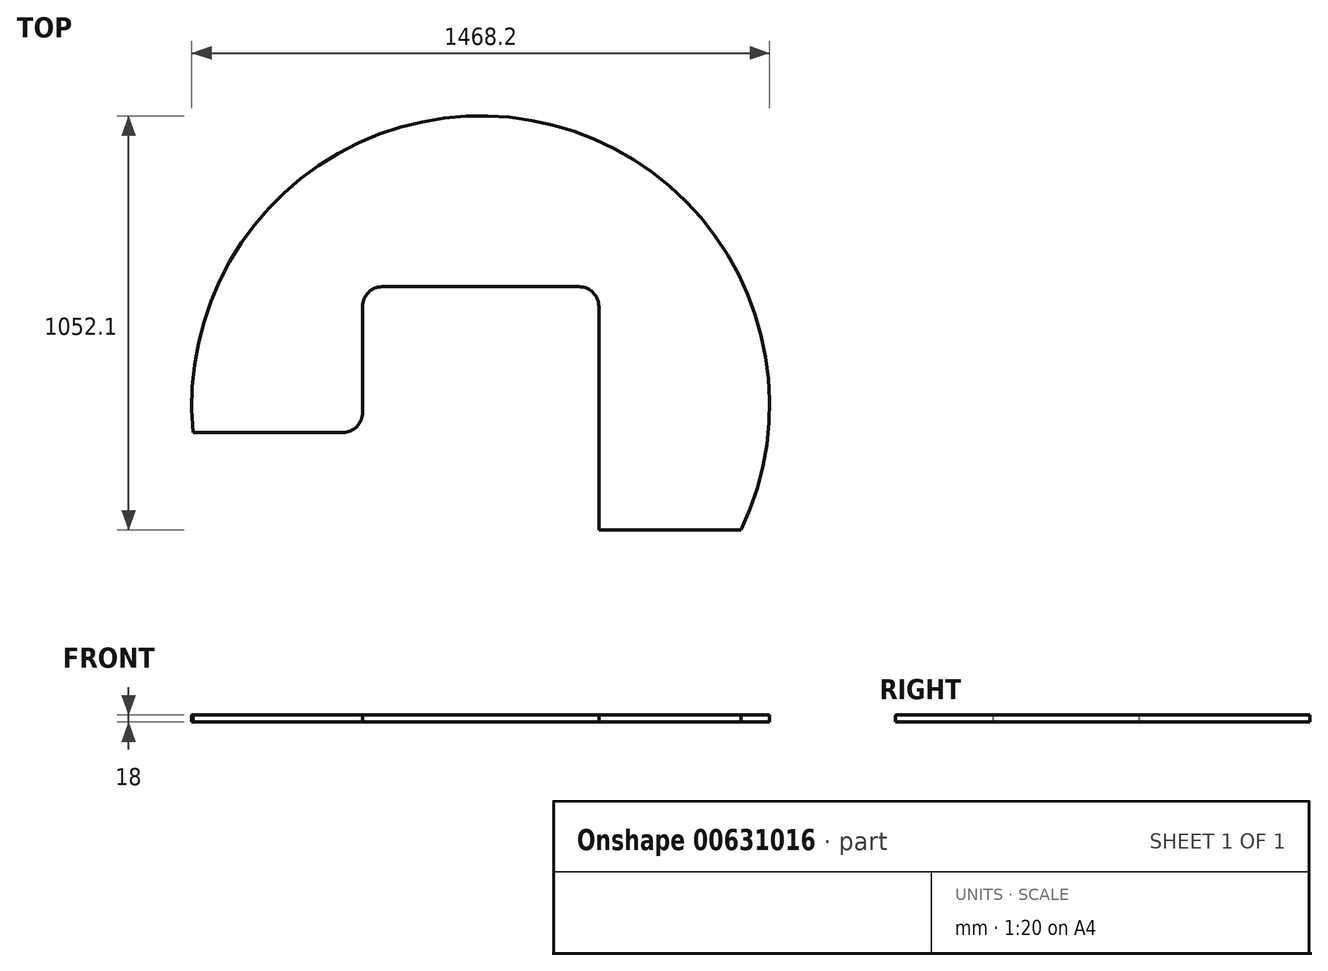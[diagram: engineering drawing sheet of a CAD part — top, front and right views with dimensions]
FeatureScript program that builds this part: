
annotation { "Feature Type Name" : "Feature", "Feature Type Description" : "" }
export const myFeature = defineFeature(function(context is Context, id is Id, definition is map)
    precondition{}
    {
        {
            var Q0;
            Q0=qCreatedBy(makeId("Top.planeOp"),FACE);
            var sketch = newSketch(context, id + "F0", { "sketchPlane" : qUnion([Q0])});
            skLineSegment(sketch, "E0.top", {"start": v(-250, 300) * mm, "end": v(250, 300) * mm});
            skLineSegment(sketch, "E0.left", {"start": v(-300, -2.1) * mm, "end": v(-300, 250) * mm});
            skLineSegment(sketch, "E0.right", {"start": v(300, -300) * mm, "end": v(300, 250) * mm});
            skPoint(sketch, "E0.middle", {"position": v(0, 0) * mm});
            skPoint(sketch, "E1.end.orphan", {"position": v(-300, -300) * mm});
            skPoint(sketch, "E2.visualSharp", {"position": v(-300, 300) * mm});
            skArc(sketch, "E2.filletArc", {"start": v(-250, 300) * mm, "mid": v(-285.36, 285.36) * mm, "end": v(-300, 250) * mm});
            skPoint(sketch, "E3.visualSharp", {"position": v(-300, -52.1) * mm});
            skPoint(sketch, "E4.visualSharp", {"position": v(300, 300) * mm});
            skArc(sketch, "E4.filletArc", {"start": v(300, 250) * mm, "mid": v(285.36, 285.36) * mm, "end": v(250, 300) * mm});
            skLineSegment(sketch, "E5", {"start": v(-300, -2.1) * mm, "end": v(-300, -2.1) * mm});
            skArc(sketch, "E6", {"start": v(670, -300) * mm, "mid": v(128.43, 722.78) * mm, "end": v(-732.34, -50.83) * mm});
            skLineSegment(sketch, "E7", {"start": v(300, -300) * mm, "end": v(300, -318) * mm});
            skLineSegment(sketch, "E8", {"start": v(300, -318) * mm, "end": v(661.65, -318) * mm});
            skLineSegment(sketch, "E9", {"start": v(-300, -2.1) * mm, "end": v(-300, -20.1) * mm});
            skArc(sketch, "E10", {"start": v(670, -300) * mm, "mid": v(665.88, -309.03) * mm, "end": v(661.65, -318) * mm});
            skLineSegment(sketch, "E11", {"start": v(-350, -70.1) * mm, "end": v(-730.74, -70.1) * mm});
            skArc(sketch, "E12", {"start": v(-732.34, -50.83) * mm, "mid": v(-731.6, -60.46) * mm, "end": v(-730.74, -70.1) * mm});
            skPoint(sketch, "E13.visualSharp", {"position": v(-300, -70.1) * mm});
            skArc(sketch, "E13.filletArc", {"start": v(-350, -70.1) * mm, "mid": v(-314.64, -55.45) * mm, "end": v(-300, -20.1) * mm});
            skSolve(sketch);
        }
        {
            var Q0;
            Q0=qSketchRegion(id+"F0",true);
            extrude(context, id + "F1", {"entities" : qUnion([Q0]), "depth" : 18 * mm, "offsetDistance" : 25 * mm});
        }
    });
